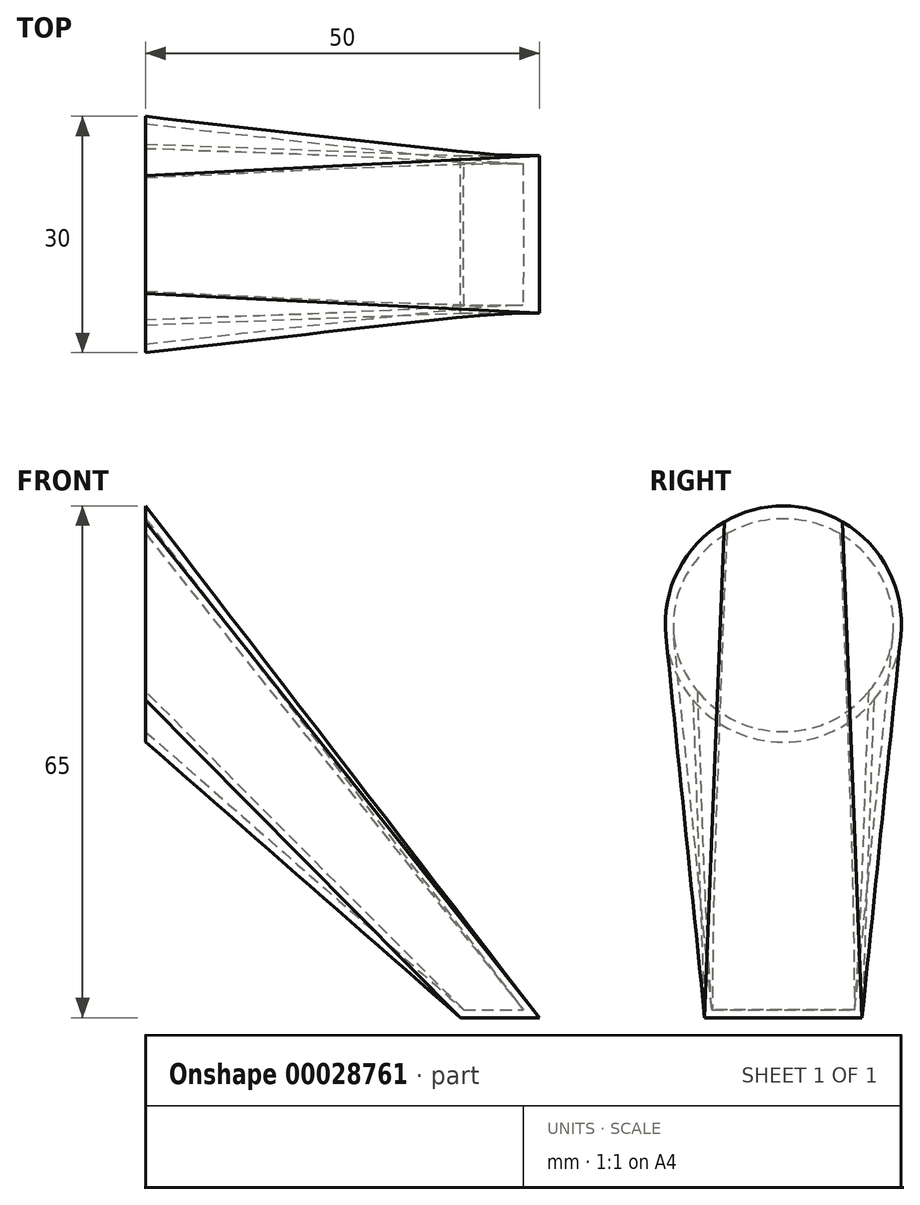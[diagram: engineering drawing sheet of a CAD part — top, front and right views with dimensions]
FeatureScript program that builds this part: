
annotation { "Feature Type Name" : "Feature", "Feature Type Description" : "" }
export const myFeature = defineFeature(function(context is Context, id is Id, definition is map)
    precondition{}
    {
        {
            var Q0;
            Q0=qCreatedBy(makeId("Right.planeOp"),FACE);
            var sketch = newSketch(context, id + "F0", { "sketchPlane" : qUnion([Q0])});
            skPoint(sketch, "E0.rect.middle", {"position": v(0, 0) * mm});
            skArc(sketch, "E1", {"start": v(-7.5, 13) * mm, "mid": v(0, -15) * mm, "end": v(7.5, 13) * mm});
            skArc(sketch, "E2", {"start": v(7.5, 13) * mm, "mid": v(0, 15) * mm, "end": v(-7.5, 13) * mm});
            skLineSegment(sketch, "E3", {"start": v(0, 0) * mm, "end": v(-7.5, 13) * mm, "construction": true});
            skLineSegment(sketch, "E4", {"start": v(0, 0) * mm, "end": v(7.5, 13) * mm, "construction": true});
            skLineSegment(sketch, "E5", {"start": v(0, 18.33) * mm, "end": v(0, -72.87) * mm, "construction": true});
            skSolve(sketch);
        }
        {
            var Q0;
            Q0=qCreatedBy(makeId("Top.planeOp"),FACE);
            cPlane(context, id + "F1", {"entities" : qUnion([Q0]), "cplaneType" : CPlaneType.OFFSET, "offset" : 50 * mm, "oppositeDirection" : true, "width" : 150 * mm, "height" : 150 * mm});
        }
        {
            var Q0;
            Q0=qCreatedBy(id+"F1.planeOp",FACE);
            var sketch = newSketch(context, id + "F2", { "sketchPlane" : qUnion([Q0])});
            skLineSegment(sketch, "E6.rect.bottom", {"start": v(40, -10) * mm, "end": v(50, -10) * mm});
            skLineSegment(sketch, "E6.rect.top", {"start": v(40, 10) * mm, "end": v(50, 10) * mm});
            skLineSegment(sketch, "E6.rect.left", {"start": v(40, -10) * mm, "end": v(40, 10) * mm});
            skLineSegment(sketch, "E6.rect.right", {"start": v(50, -10) * mm, "end": v(50, 10) * mm});
            skPoint(sketch, "E6.rect.middle", {"position": v(45, 0) * mm});
            skLineSegment(sketch, "E7", {"start": v(57.4, 0) * mm, "end": v(-33.86, 0) * mm, "construction": true});
            skSolve(sketch);
        }
        {
            var Q0;
            Q0=sQuery(id+"F2.wireOp",EDGE,"E6.rect.right");
            cPlane(context, id + "F3", {"entities" : qUnion([Q0]), "cplaneType" : CPlaneType.LINE_ANGLE, "offset" : 150 * mm, "angle" : 51.56 * degree, "width" : 150 * mm, "height" : 150 * mm});
        }
        {
            var Q0;
            Q0=qCreatedBy(id+"F3.planeOp",FACE);
            var sketch = newSketch(context, id + "F4", { "sketchPlane" : qUnion([Q0])});
            skLineSegment(sketch, "E8", {"start": v(10, -70.25) * mm, "end": v(7.5, 10.17) * mm});
            skLineSegment(sketch, "E9", {"start": v(-10, -70.25) * mm, "end": v(-7.5, 10.17) * mm});
            skSolve(sketch);
        }
        {
            var Q0;
            Q0=makeQuery(id+"F0.imprint","IMPRINT",FACE,{"disambiguationData":[TD([[makeQuery(id+"F0.imprint","IMPRINT",EDGE,{"derivedFrom":sQuery(id+"F0.wireOp",EDGE,"E1")}),1.0]])]});
            var Q1;
            Q1=makeQuery(id+"F2.imprint","IMPRINT",FACE,{"disambiguationData":[TD([[makeQuery(id+"F2.imprint","IMPRINT",EDGE,{"derivedFrom":sQuery(id+"F2.wireOp",EDGE,"E6.rect.bottom")}),1.0]])]});
            var Q2;
            Q2=sQuery(id+"F4.wireOp",EDGE,"E9");
            var Q3;
            Q3=sQuery(id+"F4.wireOp",EDGE,"E8");
            var Q4;
            Q4=sQuery(id+"F2.wireOp",VERTEX,"E6.rect.top.end");
            var Q5;
            Q5=sQuery(id+"F4.wireOp",VERTEX,"E8.end");
            loft(context, id + "F5", {"addGuides" : true, "sheetProfilesArray" : [{ "sheetProfileEntities" : qUnion([Q0]) }, { "sheetProfileEntities" : qUnion([Q1]) }], "guidesArray" : [{ "guideEntities" : qUnion([Q2]), "guideDerivativeType" : LoftGuideDerivativeType.DEFAULT, "guideDerivativeMagnitude" : 1 }, { "guideEntities" : qUnion([Q3]), "guideDerivativeType" : LoftGuideDerivativeType.DEFAULT, "guideDerivativeMagnitude" : 1 }], "connections" : [{ "connectionEntities" : qUnion([Q4, Q5]), "connectionEdgeQueries" : qUnion([]), "connectionEdgeParameters" : [] }]});
        }
        {
            var Q0;
            Q0=makeQuery(id+"F5.opLoft","CAP_FACE",FACE,{"disambiguationData":[OSD([makeQuery(id+"F0.imprint","IMPRINT",FACE,{"disambiguationData":[TD([[makeQuery(id+"F0.imprint","IMPRINT",EDGE,{"derivedFrom":sQuery(id+"F0.wireOp",EDGE,"E1")}),1.0]])]})])],"isStart":true});
            var Q1;
            Q1=makeQuery(id+"F5.opLoft","CAP_FACE",FACE,{"disambiguationData":[OSD([makeQuery(id+"F2.imprint","IMPRINT",FACE,{"disambiguationData":[TD([[makeQuery(id+"F2.imprint","IMPRINT",EDGE,{"derivedFrom":sQuery(id+"F2.wireOp",EDGE,"E6.rect.bottom")}),1.0]])]})])],"isStart":true});
            shell(context, id + "F6", {"entities" : qUnion([Q0, Q1]), "thickness" : 1 * mm});
        }
    });
